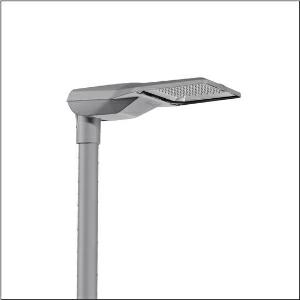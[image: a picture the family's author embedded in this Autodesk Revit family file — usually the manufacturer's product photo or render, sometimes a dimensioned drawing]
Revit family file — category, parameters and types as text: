
# Revit family: streetlight_sl_21_iq_midi___st0_5a_5xe3b41d08nb_db24
name_source: partatom
category: Lighting Fixtures
units: mm (PartAtom-declared; Revit-internal decimal feet)

## family parameters
Cut with Voids When Loaded = No
Host = Face
Light Source = No
Part Type = Normal
Room Calculation Point = No
Round Connector Dimension = Use Diameter
Shared = No

## types (1)
- --- (1 x LED, 24250 lm, 155.5 W, 4000K)
    Apparent Load = 155 VA
    CIE Flux Codes = 43 76 97 100 100
    Color Rendering = 70
    Color Temperature = 4000K
    Default Elevation = 1800 mm
    Description = Streetlight SL 21 iQ midi, mast luminaire, primary light control with lens, of PMMA, primary optical cover: cover, of toughened safety glass, transparent, light distribution: ST0.5a, light emission: direct distribution, primary light characteristic: asymmetric, installation type: post-top, side-entry, LED, High Power LED, rated luminous flux: 24.250lm, luminous efficacy: 156lm/W, light colour: 740, colour temperature: 4000K, control: Auto-Match, Temp-Guard, Lumen-Switch, Night-Set, Smart-Wire, Light-Fading, Desk-Remote (wireless, voltage-free reading and setting of iQ features in the workshop via application-optimized NFC function/RFID function), optimised constant luminous flux control (CLO 2.0), presetting dimming linear, mains connection: 230..240V, AC, 50/60Hz, start of lifetime: 156W, end of service life: 162W, reduction: 69W, luminaire housing, of diecast aluminium, powder-coated, Siteco® metallic grey (DB 702S), corrosivity category C5 mid according to DIN EN ISO 12944, please order mast flange separately, inclination adjustable: 0°, 5°, 10°, 15°, sealing non-destructively replaceable, multi-level sealing system, length: 644mm, width: 335mm, height: 110mm, mast flange for spigot size: 42mm (side-entry): 5XC10008XM4, 60/48mm (side-entry/post-top): 5XC10108XM2, 76/60mm (side-entry/post-top): 5XC10108XM1, protection rating (complete): IP66, insulation class (complete): insulation class II (safety insulation), certification: CE, ENEC, ENEC+, VDE, impact resistance: IK09, permissible operating ambient temperature for outdoor applications: -40..+50°C, standard-compliant lighting for roads and squares, packaging unit: 1 piece

Light Distribution: ST0.5a
    Height = 111 mm
    Lamp = 1 x LED
    Lamp Light Flux = 24250 lm
    Lamp Power = 155.5 W
    Lamp count = 1
    Length = 644 mm
    Luminous efficacy = 156 lm/W
    Manufacturer = Siteco
    ModVariant = No
    Model = 5XE3B41D08NB
    Number of Poles = 1
    OnlyDefault = Yes
    Power Factor = 1
    Product Name = Streetlight SL 21 iQ midi | ST0.5a
    Product group = mast luminaire | pylon top
    ProductGroupID = 6100
    Protection Class = Protection class II
    Protection Degree = IP 66
    RLX_Detail_Level = 1
    RLX_Emergency_Light_Flux = 0 lm
    RLX_Emergency_Type = 0
    RLX_Emergency_Type_DB = No
    RlxData = <blob elided: 102237 chars, md5=7d4c527e>
    Socket = socket
    Standby Power = 0 W
    System Light Flux = 24250 lm
    System Power = 155 W
    Type Comments = factory setting: luminous flux: 100 % | dim-lin: 254 | 823 mA
    Type Image = l_1004298.jpg
    URL = http://relux.com
    VarID = @adj_104429
    Voltage = 0 V
    Weight = 0.00 kg
    Width = 336 mm

## geometry (parser evidence)
native form markers: Blend x4, Sweep x10
no freeform markers — native parametric forms only
